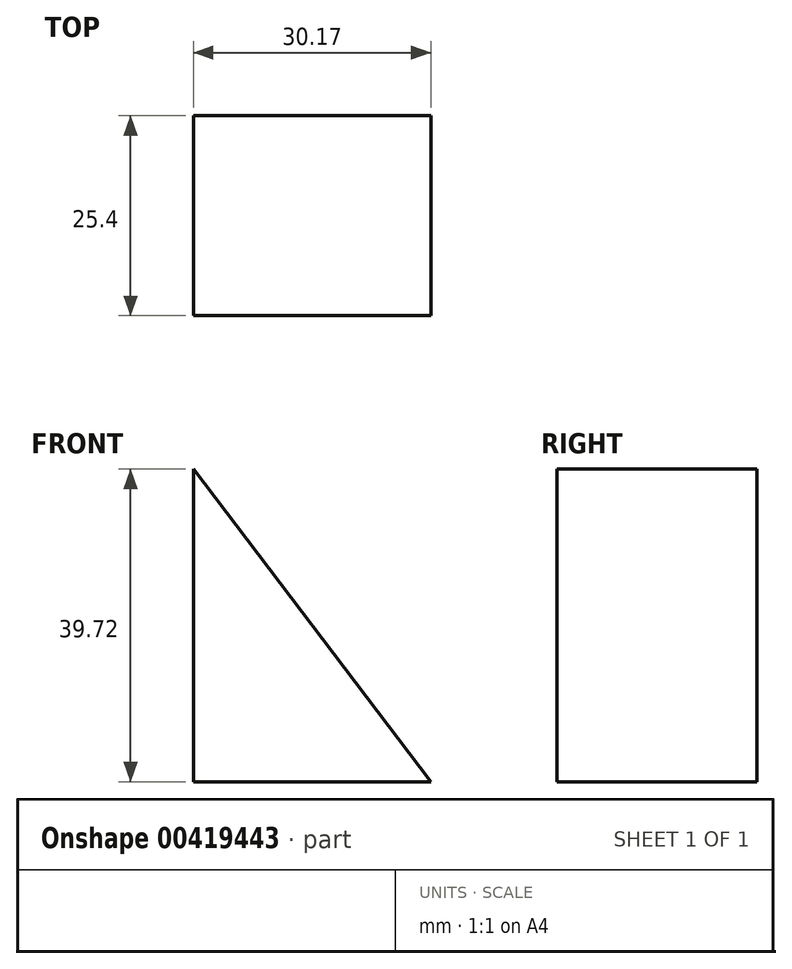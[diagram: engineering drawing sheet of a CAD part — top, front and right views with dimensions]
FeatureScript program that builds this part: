
annotation { "Feature Type Name" : "Feature", "Feature Type Description" : "" }
export const myFeature = defineFeature(function(context is Context, id is Id, definition is map)
    precondition{}
    {
        {
            var Q0;
            Q0=qCreatedBy(makeId("Front.planeOp"),FACE);
            var sketch = newSketch(context, id + "F0", { "sketchPlane" : qUnion([Q0])});
            skLineSegment(sketch, "E0", {"start": v(-30.17, 39.72) * mm, "end": v(-30.17, 0) * mm});
            skLineSegment(sketch, "E1", {"start": v(-30.17, 0) * mm, "end": v(0, 0) * mm});
            skLineSegment(sketch, "E2", {"start": v(-30.17, 39.72) * mm, "end": v(0, 0) * mm});
            skSolve(sketch);
        }
        {
            var Q0;
            Q0 = qSketchRegion(id + "F0", true);
            extrude(context, id + "F1", {"entities" : qUnion([Q0]), "depth" : 25.4 * mm});
        }
    });
